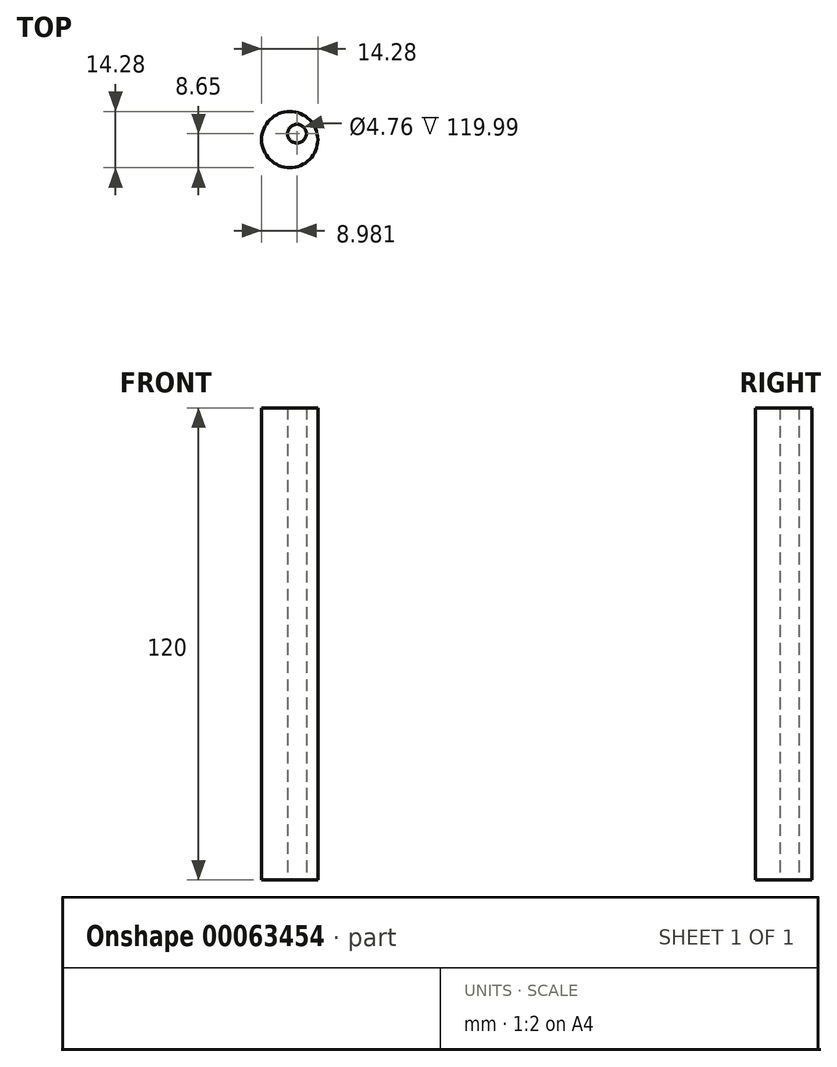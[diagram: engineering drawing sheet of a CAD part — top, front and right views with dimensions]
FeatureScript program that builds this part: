
annotation { "Feature Type Name" : "Feature", "Feature Type Description" : "" }
export const myFeature = defineFeature(function(context is Context, id is Id, definition is map)
    precondition{}
    {
        {
            var Q0;
            Q0=qCreatedBy(makeId("Top.planeOp"),FACE);
            var sketch = newSketch(context, id + "F0", { "sketchPlane" : qUnion([Q0])});
            skCircle(sketch, "E0", {"center": v(0, 0) * mm, "radius": 7.14 * mm});
            skCircle(sketch, "E1", {"center": v(1.84, 1.5) * mm, "radius": 2.38 * mm});
            skSolve(sketch);
        }
        {
            var Q0;
            Q0=makeQuery(id+"F0.imprint","IMPRINT",FACE,{"disambiguationData":[TD([[makeQuery(id+"F0.imprint","IMPRINT",EDGE,{"derivedFrom":sQuery(id+"F0.wireOp",EDGE,"E0")}),1.0]])]});
            extrude(context, id + "F1", {"entities" : qUnion([Q0]), "depth" : 120 * mm});
        }
        {
            var Q0;
            Q0=makeQuery(id+"F1.opExtrude","CAP_FACE",FACE,{"disambiguationData":[OSD([sQuery(id+"F0.wireOp",EDGE,"E0"),sQuery(id+"F0.wireOp",EDGE,"E1")])],"isStart":true});
            var sketch = newSketch(context, id + "F2", { "sketchPlane" : qUnion([Q0])});
            skSolve(sketch);
        }
        {
            var Q0;
            Q0=makeQuery(id+"F2.imprint","IMPRINT",FACE,{"disambiguationData":[TD([[makeQuery(id+"F2.imprint","IMPRINT",EDGE,{"derivedFrom":makeQuery(id+"F1.opExtrude","CAP_EDGE",EDGE,{"disambiguationData":[OSD([sQuery(id+"F0.wireOp",EDGE,"E1")])],"isStart":true})}),-1.0]])]});
            extrude(context, id + "F3", {"entities" : qUnion([Q0]), "operationType" : NewBodyOperationType.ADD, "oppositeDirection" : true, "depth" : 1 / 101.6 * mm});
        }
    });
